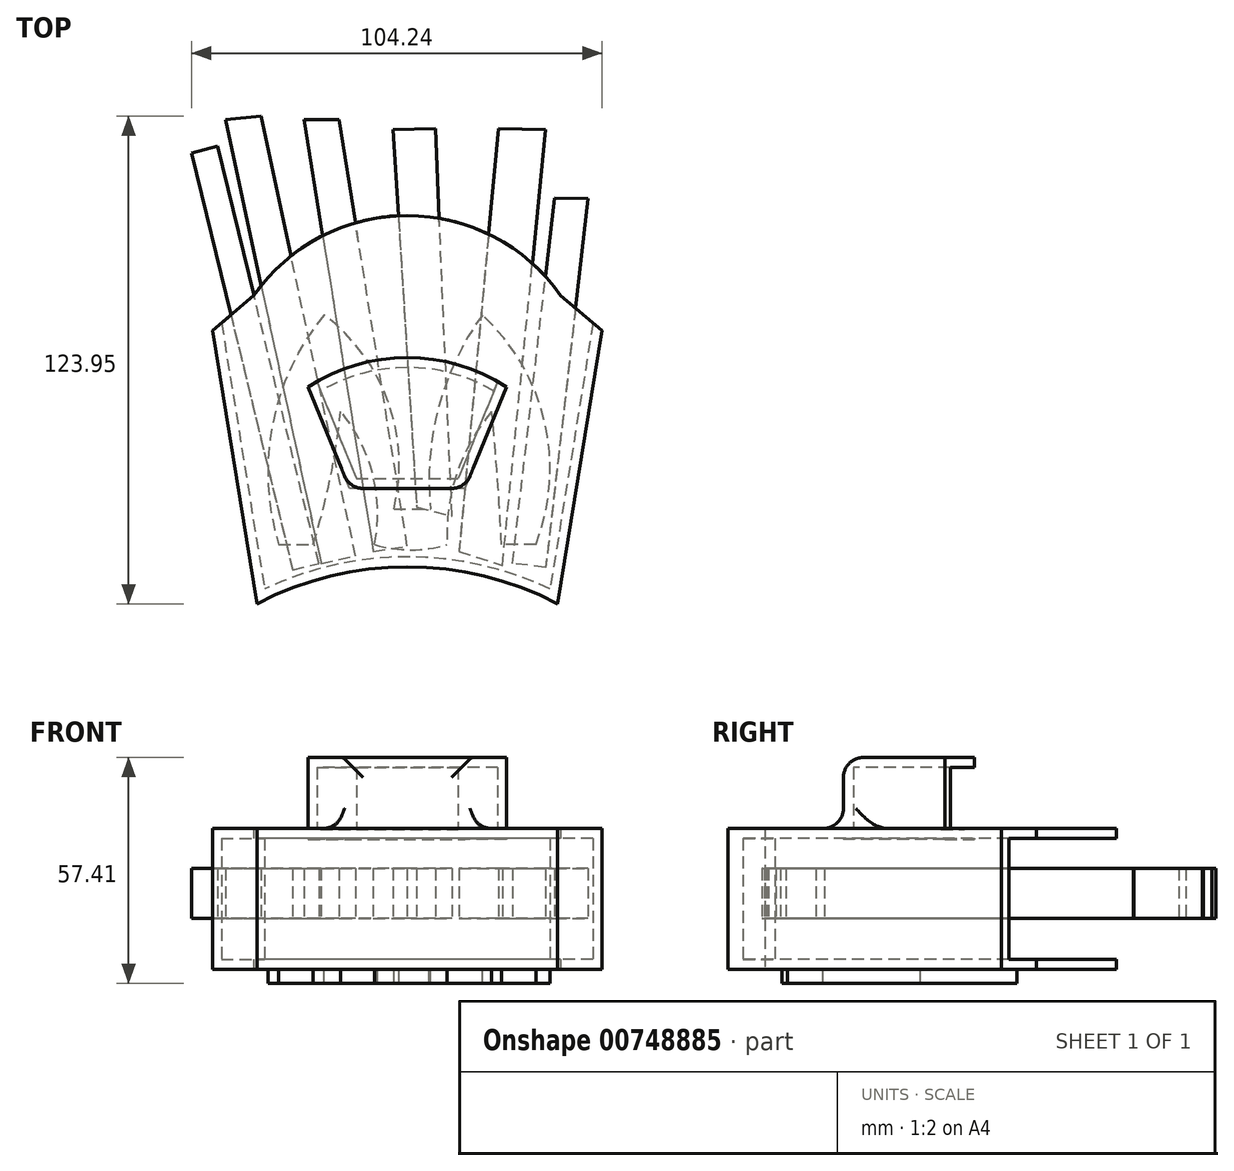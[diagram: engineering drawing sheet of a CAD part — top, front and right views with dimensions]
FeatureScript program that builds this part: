
annotation { "Feature Type Name" : "Feature", "Feature Type Description" : "" }
export const myFeature = defineFeature(function(context is Context, id is Id, definition is map)
    precondition{}
    {
        {
            var Q0;
            Q0=qCreatedBy(makeId("Top.planeOp"),FACE);
            var sketch = newSketch(context, id + "F0", { "sketchPlane" : qUnion([Q0])});
            skLineSegment(sketch, "E0", {"start": v(-49.46, 20.56) * mm, "end": v(-38.2, -48.88) * mm});
            skLineSegment(sketch, "E1.MirrorCS", {"start": v(49.46, 20.56) * mm, "end": v(38.2, -48.88) * mm});
            skArc(sketch, "E2", {"start": v(38.2, -48.88) * mm, "mid": v(0, -39.45) * mm, "end": v(-38.2, -48.88) * mm});
            skLineSegment(sketch, "E3", {"start": v(-49.46, 20.56) * mm, "end": v(-38.99, 29.48) * mm});
            skLineSegment(sketch, "E4.MirrorCS", {"start": v(49.46, 20.56) * mm, "end": v(38.99, 29.48) * mm});
            skArc(sketch, "E5", {"start": v(38.99, 29.48) * mm, "mid": v(0, 49.81) * mm, "end": v(-38.99, 29.48) * mm});
            skSolve(sketch);
        }
        {
            var Q0;
            Q0 = qSketchRegion(id + "F0", true);
            extrude(context, id + "F1", {"entities" : qUnion([Q0]), "depth" : 35.81 * mm, "offsetDistance" : 25.4 * mm});
        }
        {
            var Q0;
            Q0=makeQuery(id+"F1.opExtrude","SWEPT_FACE",FACE,{"disambiguationData":[OSD([sQuery(id+"F0.wireOp",EDGE,"E5")])]});
            var Q1;
            Q1=makeQuery(id+"F1.opExtrude","SWEPT_FACE",FACE,{"disambiguationData":[OSD([sQuery(id+"F0.wireOp",EDGE,"E3")])]});
            var Q2;
            Q2=makeQuery(id+"F1.opExtrude","SWEPT_FACE",FACE,{"disambiguationData":[OSD([sQuery(id+"F0.wireOp",EDGE,"E4.MirrorCS")])]});
            shell(context, id + "F2", {"entities" : qUnion([Q0, Q1, Q2]), "thickness" : 2.54 * mm});
        }
        {
            var Q0;
            Q0=qCreatedBy(makeId("Top.planeOp"),FACE);
            var sketch = newSketch(context, id + "F3", { "sketchPlane" : qUnion([Q0])});
            skLineSegment(sketch, "E6", {"start": v(-25.17, 6.26) * mm, "end": v(-14.65, -19.53) * mm});
            skLineSegment(sketch, "E7.MirrorCS", {"start": v(25.17, 6.26) * mm, "end": v(14.65, -19.53) * mm});
            skLineSegment(sketch, "E8", {"start": v(-14.65, -19.53) * mm, "end": v(14.65, -19.53) * mm});
            skArc(sketch, "E9", {"start": v(25.17, 6.26) * mm, "mid": v(0, 13.75) * mm, "end": v(-25.17, 6.26) * mm});
            skSolve(sketch);
        }
        {
            var Q0;
            Q0 = qSketchRegion(id + "F3", true);
            extrude(context, id + "F4", {"entities" : qUnion([Q0]), "operationType" : NewBodyOperationType.ADD, "depth" : 53.85 * mm, "offsetDistance" : 25.4 * mm, "hasSecondDirection" : true, "secondDirectionOppositeDirection" : false, "secondDirectionDepth" : 33.02 * mm});
        }
        {
            var Q0;
            {var subQ0=sQuery(id+"F3.wireOp",EDGE,"E7.MirrorCS");var subQ1=sQuery(id+"F3.wireOp",EDGE,"E6");var subQ2=sQuery(id+"F3.wireOp",EDGE,"E9");Q0=makeQuery(id+"F4.boolean.opBoolean","SPLIT",FACE,{"disambiguationData":[TD([makeQuery(id+"F4.opExtrude","CAP_FACE",FACE,{"disambiguationData":[OSD([subQ1,subQ0,sQuery(id+"F3.wireOp",EDGE,"E8"),subQ2])],"isStart":false})])],"derivedFrom":makeQuery(id+"F4.opExtrude","SWEPT_FACE",FACE,{"disambiguationData":[OSD([subQ2])]})});}
            shell(context, id + "F5", {"entities" : qUnion([Q0]), "thickness" : 2.54 * mm});
        }
        {
            var Q0;
            {var subQ0=sQuery(id+"F3.wireOp",EDGE,"E7.MirrorCS");var subQ1=sQuery(id+"F3.wireOp",EDGE,"E6");var subQ2=sQuery(id+"F3.wireOp",EDGE,"E8");Q0=makeQuery(id+"F4.boolean.opBoolean","SPLIT",FACE,{"disambiguationData":[TD([makeQuery(id+"F4.opExtrude","CAP_FACE",FACE,{"disambiguationData":[OSD([subQ1,subQ0,subQ2,sQuery(id+"F3.wireOp",EDGE,"E9")])],"isStart":false})])],"derivedFrom":makeQuery(id+"F4.opExtrude","SWEPT_FACE",FACE,{"disambiguationData":[OSD([subQ2])]})});}
            fillet(context, id + "F6", {"entities" : qUnion([Q0]), "radius" : 5.08 * mm, "tangentPropagation" : true, "allowEdgeOverflow" : false});
        }
        {
            var Q0;
            Q0=qCreatedBy(makeId("Top.planeOp"),FACE);
            var sketch = newSketch(context, id + "F7", { "sketchPlane" : qUnion([Q0])});
            skLineSegment(sketch, "E10", {"start": v(-54.78, 65.67) * mm, "end": v(-29.1, -40.2) * mm});
            skLineSegment(sketch, "E11", {"start": v(-29.1, -40.2) * mm, "end": v(-22.45, -38.59) * mm});
            skLineSegment(sketch, "E12", {"start": v(-22.45, -38.59) * mm, "end": v(-48.17, 67.42) * mm});
            skLineSegment(sketch, "E13", {"start": v(-48.17, 67.42) * mm, "end": v(-54.78, 65.67) * mm});
            skLineSegment(sketch, "E14", {"start": v(-46.2, 74.13) * mm, "end": v(-21.91, -38.57) * mm});
            skLineSegment(sketch, "E15", {"start": v(-21.91, -38.57) * mm, "end": v(-13.1, -36.67) * mm});
            skLineSegment(sketch, "E16", {"start": v(-13.1, -36.67) * mm, "end": v(-37.2, 75.07) * mm});
            skLineSegment(sketch, "E17", {"start": v(-37.2, 75.07) * mm, "end": v(-46.2, 74.13) * mm});
            skLineSegment(sketch, "E18", {"start": v(-26.17, 74.13) * mm, "end": v(-8.64, -35.56) * mm});
            skLineSegment(sketch, "E19", {"start": v(-8.64, -35.56) * mm, "end": v(0, -34.18) * mm});
            skLineSegment(sketch, "E20", {"start": v(0, -34.18) * mm, "end": v(-17.3, 74.13) * mm});
            skLineSegment(sketch, "E21", {"start": v(-17.3, 74.13) * mm, "end": v(-26.17, 74.13) * mm});
            skLineSegment(sketch, "E22", {"start": v(-3.63, 71.62) * mm, "end": v(2.38, -24.3) * mm});
            skLineSegment(sketch, "E23", {"start": v(2.38, -24.3) * mm, "end": v(11.4, -26.54) * mm});
            skLineSegment(sketch, "E24", {"start": v(11.4, -26.54) * mm, "end": v(7.14, 71.87) * mm});
            skLineSegment(sketch, "E25", {"start": v(7.14, 71.87) * mm, "end": v(-3.63, 71.62) * mm});
            skLineSegment(sketch, "E26", {"start": v(23.16, 71.87) * mm, "end": v(13.15, -35.56) * mm});
            skLineSegment(sketch, "E27", {"start": v(13.15, -35.56) * mm, "end": v(24.17, -39.07) * mm});
            skLineSegment(sketch, "E28", {"start": v(24.17, -39.07) * mm, "end": v(35.18, 71.62) * mm});
            skLineSegment(sketch, "E29", {"start": v(35.18, 71.62) * mm, "end": v(23.16, 71.87) * mm});
            skLineSegment(sketch, "E30", {"start": v(45.95, 54.1) * mm, "end": v(35.18, -39.57) * mm});
            skLineSegment(sketch, "E31", {"start": v(35.18, -39.57) * mm, "end": v(26.74, -38.6) * mm});
            skLineSegment(sketch, "E32", {"start": v(26.74, -38.6) * mm, "end": v(37.42, 54.26) * mm});
            skLineSegment(sketch, "E33", {"start": v(37.42, 54.26) * mm, "end": v(45.95, 54.1) * mm});
            skSolve(sketch);
        }
        {
            var Q0;
            Q0 = qSketchRegion(id + "F7", true);
            extrude(context, id + "F8", {"entities" : qUnion([Q0]), "operationType" : NewBodyOperationType.ADD, "depth" : 25.65 * mm, "offsetDistance" : 25.4 * mm, "hasSecondDirection" : true, "secondDirectionOppositeDirection" : false, "secondDirectionDepth" : 12.95 * mm});
        }
        {
            var Q0;
            Q0=qCreatedBy(makeId("Top.planeOp"),FACE);
            var sketch = newSketch(context, id + "F9", { "sketchPlane" : qUnion([Q0])});
            skLineSegment(sketch, "E34", {"start": v(-32.68, -33.8) * mm, "end": v(-23.92, -33.8) * mm});
            skLineSegment(sketch, "E35.MirrorCS", {"start": v(32.68, -33.8) * mm, "end": v(23.92, -33.8) * mm});
            skLineSegment(sketch, "E36", {"start": v(-3.38, -24.8) * mm, "end": v(5.88, -24.8) * mm});
            skArc(sketch, "E37", {"start": v(-21.16, 24.54) * mm, "mid": v(-34.22, -3.2) * mm, "end": v(-32.68, -33.8) * mm});
            skArc(sketch, "E38", {"start": v(-3.38, -24.8) * mm, "mid": v(-4.85, 2.55) * mm, "end": v(-21.16, 24.54) * mm});
            skArc(sketch, "E39", {"start": v(-3.38, -24.8) * mm, "mid": v(1.25, -25.88) * mm, "end": v(5.88, -24.8) * mm});
            skArc(sketch, "E40", {"start": v(19.07, 24.54) * mm, "mid": v(7.97, 1.08) * mm, "end": v(5.88, -24.8) * mm});
            skArc(sketch, "E41", {"start": v(32.68, -33.8) * mm, "mid": v(34.88, -2.53) * mm, "end": v(19.07, 24.54) * mm});
            skArc(sketch, "E42", {"start": v(23.92, -33.8) * mm, "mid": v(22.94, -16.89) * mm, "end": v(21.45, 0) * mm});
            skArc(sketch, "E43", {"start": v(-23.92, -33.8) * mm, "mid": v(-19.58, -17.07) * mm, "end": v(-16.9, 0) * mm});
            skArc(sketch, "E44", {"start": v(-8.33, -33.8) * mm, "mid": v(-8.77, -15.93) * mm, "end": v(-16.9, 0) * mm});
            skArc(sketch, "E45", {"start": v(21.45, 0) * mm, "mid": v(12.57, -15.82) * mm, "end": v(10.13, -33.8) * mm});
            skArc(sketch, "E46", {"start": v(-8.33, -33.8) * mm, "mid": v(0.9, -35.14) * mm, "end": v(10.13, -33.8) * mm});
            skSolve(sketch);
        }
        {
            var Q0;
            Q0 = qSketchRegion(id + "F9", true);
            extrude(context, id + "F10", {"entities" : qUnion([Q0]), "oppositeDirection" : true, "depth" : 3.56 * mm, "offsetDistance" : 25.4 * mm});
        }
    });
